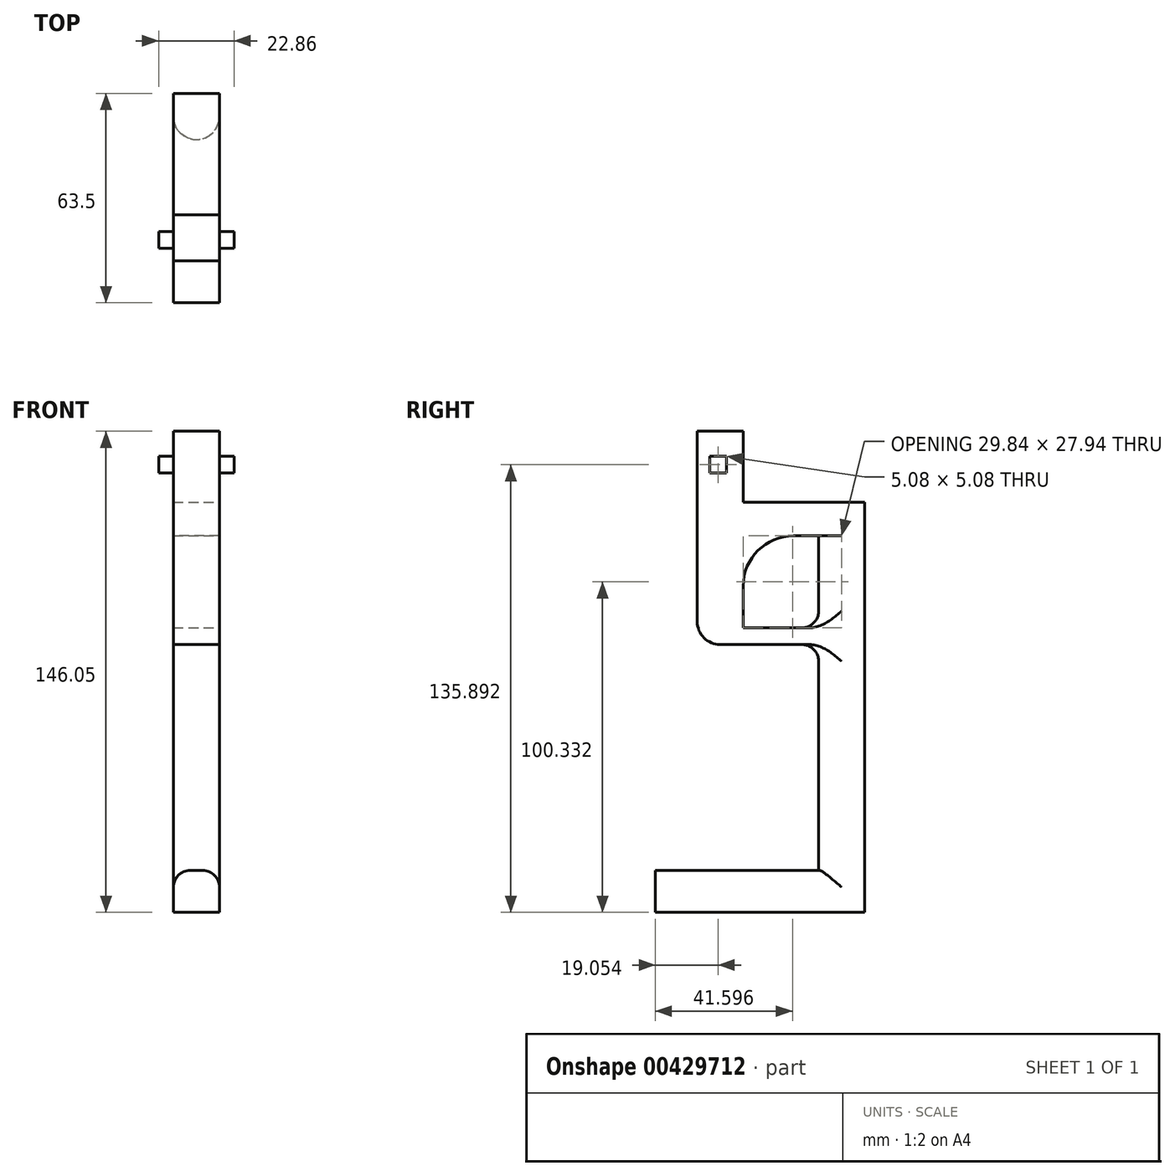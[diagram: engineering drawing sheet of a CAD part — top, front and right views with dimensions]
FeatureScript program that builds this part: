
annotation { "Feature Type Name" : "Feature", "Feature Type Description" : "" }
export const myFeature = defineFeature(function(context is Context, id is Id, definition is map)
    precondition{}
    {
        {
            var Q0;
            Q0=qCreatedBy(makeId("Right.planeOp"),FACE);
            var sketch = newSketch(context, id + "F0", { "sketchPlane" : qUnion([Q0])});
            skLineSegment(sketch, "E0.bottom", {"start": v(-42.7, -17.5) * mm, "end": v(20.8, -17.5) * mm});
            skLineSegment(sketch, "E0.top", {"start": v(-42.7, -30.2) * mm, "end": v(20.8, -30.2) * mm});
            skLineSegment(sketch, "E0.left", {"start": v(-42.7, -17.5) * mm, "end": v(-42.7, -30.2) * mm});
            skLineSegment(sketch, "E0.right", {"start": v(20.8, -17.5) * mm, "end": v(20.8, -30.2) * mm});
            skSolve(sketch);
        }
        {
            var Q0;
            Q0=makeQuery(id+"F0.imprint","IMPRINT",FACE,{"disambiguationData":[TD([[makeQuery(id+"F0.imprint","IMPRINT",EDGE,{"derivedFrom":sQuery(id+"F0.wireOp",EDGE,"E0.bottom")}),-1.0]])]});
            extrude(context, id + "F1", {"entities" : qUnion([Q0]), "endBound" : BoundingType.SYMMETRIC, "depth" : 13.97 * mm});
        }
        {
            var Q0;
            Q0=makeQuery(id+"F1.opExtrude","SWEPT_FACE",FACE,{"disambiguationData":[OSD([sQuery(id+"F0.wireOp",EDGE,"E0.bottom")])]});
            var sketch = newSketch(context, id + "F2", { "sketchPlane" : qUnion([Q0])});
            skCircle(sketch, "E1", {"center": v(0, 13.82) * mm, "radius": 6.99 * mm});
            skSolve(sketch);
        }
        {
            var Q0;
            {var subQ0=sQuery(id+"F2.wireOp",EDGE,"E1");var subQ1=sQuery(id+"F0.wireOp",EDGE,"E0.bottom");var subQ3=makeQuery(id+"F2.imprint","INTERSECT",VERTEX,{"derivedFrom":[makeQuery(id+"F1.opExtrude","CAP_EDGE",EDGE,{"disambiguationData":[OSD([subQ1])],"isStart":false}),subQ0]});Q0=makeQuery(id+"F2.imprint","IMPRINT",FACE,{"disambiguationData":[TD([[makeQuery(id+"F2.imprint","IMPRINT",EDGE,{"disambiguationData":[TD([[subQ3,1.0]])],"derivedFrom":subQ0}),1.0]])]});}
            extrude(context, id + "F3", {"entities" : qUnion([Q0]), "operationType" : NewBodyOperationType.ADD, "depth" : 101.6 * mm});
        }
        {
            var Q0;
            Q0=qCreatedBy(makeId("Right.planeOp"),FACE);
            var sketch = newSketch(context, id + "F4", { "sketchPlane" : qUnion([Q0])});
            skLineSegment(sketch, "E2.bottom", {"start": v(-30, 56.16) * mm, "end": v(20.8, 56.16) * mm});
            skLineSegment(sketch, "E2.top", {"start": v(-30, 51.08) * mm, "end": v(20.8, 51.08) * mm});
            skLineSegment(sketch, "E2.left", {"start": v(-30, 56.16) * mm, "end": v(-30, 51.08) * mm});
            skLineSegment(sketch, "E2.right", {"start": v(20.8, 56.16) * mm, "end": v(20.8, 51.08) * mm});
            skLineSegment(sketch, "E3.bottom", {"start": v(-30, 94.26) * mm, "end": v(20.8, 94.26) * mm});
            skLineSegment(sketch, "E3.top", {"start": v(-30, 84.1) * mm, "end": v(20.8, 84.1) * mm});
            skLineSegment(sketch, "E3.left", {"start": v(-30, 94.26) * mm, "end": v(-30, 84.1) * mm});
            skLineSegment(sketch, "E3.right", {"start": v(20.8, 94.26) * mm, "end": v(20.8, 84.1) * mm});
            skSolve(sketch);
        }
        {
            var Q0;
            Q0=makeQuery(id+"F4.imprint","IMPRINT",FACE,{"disambiguationData":[TD([[makeQuery(id+"F4.imprint","IMPRINT",EDGE,{"derivedFrom":sQuery(id+"F4.wireOp",EDGE,"E2.bottom")}),-1.0]])]});
            var Q1;
            Q1=makeQuery(id+"F4.imprint","IMPRINT",FACE,{"disambiguationData":[TD([[makeQuery(id+"F4.imprint","IMPRINT",EDGE,{"derivedFrom":sQuery(id+"F4.wireOp",EDGE,"E3.bottom")}),-1.0]])]});
            extrude(context, id + "F5", {"entities" : qUnion([Q0, Q1]), "operationType" : NewBodyOperationType.ADD, "endBound" : BoundingType.SYMMETRIC, "depth" : 13.97 * mm});
        }
        {
            var Q0;
            Q0=makeQuery(id+"F5.opExtrude","SWEPT_FACE",FACE,{"disambiguationData":[OSD([sQuery(id+"F4.wireOp",EDGE,"E3.bottom")])]});
            var sketch = newSketch(context, id + "F6", { "sketchPlane" : qUnion([Q0])});
            skLineSegment(sketch, "E4.bottom", {"start": v(6.99, -30) * mm, "end": v(-6.99, -30) * mm});
            skLineSegment(sketch, "E4.top", {"start": v(6.99, -16.03) * mm, "end": v(-6.99, -16.03) * mm});
            skLineSegment(sketch, "E4.left", {"start": v(6.99, -30) * mm, "end": v(6.98, -16.03) * mm});
            skLineSegment(sketch, "E4.right", {"start": v(-6.99, -30) * mm, "end": v(-6.99, -16.03) * mm});
            skSolve(sketch);
        }
        {
            var Q0;
            Q0=makeQuery(id+"F6.imprint","IMPRINT",FACE,{"disambiguationData":[TD([[makeQuery(id+"F6.imprint","IMPRINT",EDGE,{"derivedFrom":sQuery(id+"F6.wireOp",EDGE,"E4.bottom")}),-1.0]])]});
            var Q1;
            {var subQ0=sQuery(id+"F4.wireOp",EDGE,"E2.right");var subQ1=sQuery(id+"F4.wireOp",EDGE,"E2.left");var subQ2=sQuery(id+"F4.wireOp",EDGE,"E2.top");var subQ3=sQuery(id+"F4.wireOp",EDGE,"E2.bottom");var subQ4=makeQuery(id+"F5.opExtrude","SWEPT_FACE",FACE,{"disambiguationData":[OSD([subQ3])]});Q1=makeQuery(id+"F5.boolean.opBoolean","SPLIT",FACE,{"disambiguationData":[TD([makeQuery(id+"F3.opExtrude","SWEPT_FACE",FACE,{"disambiguationData":[OSD([sQuery(id+"F2.wireOp",EDGE,"E1")])]}),subQ4,makeQuery(id+"F5.opExtrude","CAP_FACE",FACE,{"disambiguationData":[OSD([subQ3,subQ2,subQ1,subQ0])],"isStart":true}),makeQuery(id+"F5.opExtrude","CAP_FACE",FACE,{"disambiguationData":[OSD([subQ3,subQ2,subQ1,subQ0])],"isStart":false}),makeQuery(id+"F5.opExtrude","SWEPT_FACE",FACE,{"disambiguationData":[OSD([subQ1])]})])],"derivedFrom":subQ4});}
            extrude(context, id + "F7", {"entities" : qUnion([Q0]), "operationType" : NewBodyOperationType.ADD, "endBound" : BoundingType.UP_TO_SURFACE, "oppositeDirection" : true, "endBoundEntityFace" : qUnion([Q1]), "depth" : 25.4 * mm});
        }
        {
            var Q0;
            Q0=makeQuery(id+"F1.opExtrude","CAP_EDGE",EDGE,{"disambiguationData":[OSD([sQuery(id+"F0.wireOp",EDGE,"E0.right")])],"isStart":false});
            var Q1;
            Q1=makeQuery(id+"F1.opExtrude","CAP_EDGE",EDGE,{"disambiguationData":[OSD([sQuery(id+"F0.wireOp",EDGE,"E0.right")])],"isStart":true});
            var Q2;
            Q2=makeQuery(id+"F5.opExtrude","CAP_EDGE",EDGE,{"disambiguationData":[OSD([sQuery(id+"F4.wireOp",EDGE,"E3.right")])],"isStart":false});
            var Q3;
            Q3=makeQuery(id+"F5.opExtrude","CAP_EDGE",EDGE,{"disambiguationData":[OSD([sQuery(id+"F4.wireOp",EDGE,"E3.right")])],"isStart":true});
            var Q4;
            Q4=makeQuery(id+"F5.opExtrude","CAP_EDGE",EDGE,{"disambiguationData":[OSD([sQuery(id+"F4.wireOp",EDGE,"E2.right")])],"isStart":false});
            var Q5;
            Q5=makeQuery(id+"F5.opExtrude","CAP_EDGE",EDGE,{"disambiguationData":[OSD([sQuery(id+"F4.wireOp",EDGE,"E2.right")])],"isStart":true});
            var Q6;
            Q6=makeQuery(id+"F5.opExtrude","SWEPT_EDGE",EDGE,{"disambiguationData":[OSD([sQuery(id+"F4.wireOp",EDGE,"E2.top"),sQuery(id+"F4.wireOp",EDGE,"E2.left")])]});
            fillet(context, id + "F8", {"entities" : qUnion([Q0, Q1, Q2, Q3, Q4, Q5, Q6]), "radius" : 7 * mm, "tangentPropagation" : true, "allowEdgeOverflow" : false});
        }
        {
            var Q0;
            Q0=makeQuery(id+"F5.boolean.opBoolean","INTERSECT",EDGE,{"disambiguationData":[OD(2.0)],"derivedFrom":[makeQuery(id+"F3.opExtrude","SWEPT_FACE",FACE,{"disambiguationData":[OSD([sQuery(id+"F2.wireOp",EDGE,"E1")])]}),makeQuery(id+"F5.opExtrude","SWEPT_FACE",FACE,{"disambiguationData":[OSD([sQuery(id+"F4.wireOp",EDGE,"E2.bottom")])]})]});
            var Q1;
            {var subQ0=sQuery(id+"F2.wireOp",EDGE,"E1");var subQ1=sQuery(id+"F4.wireOp",EDGE,"E3.right");var subQ2=sQuery(id+"F4.wireOp",EDGE,"E3.left");var subQ3=sQuery(id+"F4.wireOp",EDGE,"E3.top");var subQ4=sQuery(id+"F4.wireOp",EDGE,"E3.bottom");Q1=makeQuery(id+"F5.boolean.opBoolean","SPLIT",EDGE,{"disambiguationData":[TD([makeQuery(id+"F3.opExtrude","SWEPT_FACE",FACE,{"disambiguationData":[OSD([subQ0])]}),makeQuery(id+"F5.opExtrude","CAP_FACE",FACE,{"disambiguationData":[OSD([subQ4,subQ3,subQ2,subQ1])],"isStart":true}),makeQuery(id+"F5.opExtrude","CAP_FACE",FACE,{"disambiguationData":[OSD([subQ4,subQ3,subQ2,subQ1])],"isStart":false}),makeQuery(id+"F5.opExtrude","SWEPT_FACE",FACE,{"disambiguationData":[OSD([subQ3])]})])],"derivedFrom":makeQuery(id+"F3.opExtrude","CAP_EDGE",EDGE,{"disambiguationData":[OSD([subQ0])],"isStart":false})});}
            var Q2;
            Q2=makeQuery(id+"F5.boolean.opBoolean","INTERSECT",EDGE,{"disambiguationData":[OD(2.0)],"derivedFrom":[makeQuery(id+"F3.opExtrude","SWEPT_FACE",FACE,{"disambiguationData":[OSD([sQuery(id+"F2.wireOp",EDGE,"E1")])]}),makeQuery(id+"F5.opExtrude","SWEPT_FACE",FACE,{"disambiguationData":[OSD([sQuery(id+"F4.wireOp",EDGE,"E2.top")])]})]});
            var Q3;
            {var subQ0=sQuery(id+"F0.wireOp",EDGE,"E0.bottom");var subQ1=sQuery(id+"F0.wireOp",EDGE,"E0.left");Q3=makeQuery(id+"F3.boolean.opBoolean","SPLIT",EDGE,{"disambiguationData":[TD([makeQuery(id+"F1.opExtrude","SWEPT_FACE",FACE,{"disambiguationData":[OSD([subQ1])]})])],"derivedFrom":makeQuery(id+"F1.opExtrude","CAP_EDGE",EDGE,{"disambiguationData":[OSD([subQ0])],"isStart":false})});}
            var Q4;
            {var subQ0=sQuery(id+"F0.wireOp",EDGE,"E0.bottom");var subQ1=sQuery(id+"F0.wireOp",EDGE,"E0.left");Q4=makeQuery(id+"F3.boolean.opBoolean","SPLIT",EDGE,{"disambiguationData":[TD([makeQuery(id+"F1.opExtrude","SWEPT_FACE",FACE,{"disambiguationData":[OSD([subQ1])]})])],"derivedFrom":makeQuery(id+"F1.opExtrude","CAP_EDGE",EDGE,{"disambiguationData":[OSD([subQ0])],"isStart":true})});}
            fillet(context, id + "F9", {"entities" : qUnion([Q0, Q1, Q2, Q3, Q4]), "radius" : 5.08 * mm, "tangentPropagation" : true, "allowEdgeOverflow" : false});
        }
        {
            var Q0;
            Q0 = qSketchRegion(id + "F6", true);
            extrude(context, id + "F10", {"entities" : qUnion([Q0]), "operationType" : NewBodyOperationType.ADD, "depth" : 21.59 * mm});
        }
        {
            var Q0;
            Q0=qCreatedBy(makeId("Right.planeOp"),FACE);
            var sketch = newSketch(context, id + "F11", { "sketchPlane" : qUnion([Q0])});
            skLineSegment(sketch, "E5.bottom", {"start": v(-26.19, 108.23) * mm, "end": v(-21.1, 108.23) * mm});
            skLineSegment(sketch, "E5.top", {"start": v(-26.19, 103.15) * mm, "end": v(-21.1, 103.15) * mm});
            skLineSegment(sketch, "E5.left", {"start": v(-26.19, 108.23) * mm, "end": v(-26.19, 103.15) * mm});
            skLineSegment(sketch, "E5.right", {"start": v(-21.1, 108.23) * mm, "end": v(-21.1, 103.15) * mm});
            skSolve(sketch);
        }
        {
            var Q0;
            Q0 = qSketchRegion(id + "F11", true);
            extrude(context, id + "F12", {"entities" : qUnion([Q0]), "operationType" : NewBodyOperationType.ADD, "endBound" : BoundingType.SYMMETRIC, "depth" : 22.86 * mm});
        }
        {
            var Q0;
            Q0=makeQuery(id+"F5.opExtrude","SWEPT_FACE",FACE,{"disambiguationData":[OSD([sQuery(id+"F4.wireOp",EDGE,"E3.bottom")])]});
            var sketch = newSketch(context, id + "F13", { "sketchPlane" : qUnion([Q0])});
            skLineSegment(sketch, "E6.bottom", {"start": v(-6.99, 20.8) * mm, "end": v(6.99, 20.8) * mm});
            skLineSegment(sketch, "E6.top", {"start": v(-6.99, 13.82) * mm, "end": v(6.99, 13.82) * mm});
            skLineSegment(sketch, "E6.left", {"start": v(-6.99, 20.8) * mm, "end": v(-6.99, 13.82) * mm});
            skLineSegment(sketch, "E6.right", {"start": v(6.99, 20.8) * mm, "end": v(6.99, 13.82) * mm});
            skSolve(sketch);
        }
        {
            var Q0;
            Q0 = qSketchRegion(id + "F13", true);
            var Q1;
            Q1=makeQuery(id+"F1.opExtrude","SWEPT_FACE",FACE,{"disambiguationData":[OSD([sQuery(id+"F0.wireOp",EDGE,"E0.top")])]});
            extrude(context, id + "F14", {"entities" : qUnion([Q0]), "operationType" : NewBodyOperationType.ADD, "endBound" : BoundingType.UP_TO_SURFACE, "oppositeDirection" : true, "endBoundEntityFace" : qUnion([Q1]), "depth" : 25.4 * mm});
        }
        {
            var Q0;
            {var subQ0=sQuery(id+"F4.wireOp",EDGE,"E3.top");var subQ1=makeQuery(id+"F5.opExtrude","SWEPT_FACE",FACE,{"disambiguationData":[OSD([subQ0])]});var subQ2=sQuery(id+"F4.wireOp",EDGE,"E3.right");var subQ3=sQuery(id+"F4.wireOp",EDGE,"E3.left");var subQ4=sQuery(id+"F4.wireOp",EDGE,"E3.bottom");Q0=makeQuery(id+"F7.boolean.opBoolean","INTERSECT",EDGE,{"derivedFrom":[makeQuery(id+"F5.boolean.opBoolean","SPLIT",FACE,{"disambiguationData":[TD([makeQuery(id+"F3.opExtrude","SWEPT_FACE",FACE,{"disambiguationData":[OSD([sQuery(id+"F2.wireOp",EDGE,"E1")])]}),makeQuery(id+"F5.opExtrude","CAP_FACE",FACE,{"disambiguationData":[OSD([subQ4,subQ0,subQ3,subQ2])],"isStart":true}),makeQuery(id+"F5.opExtrude","CAP_FACE",FACE,{"disambiguationData":[OSD([subQ4,subQ0,subQ3,subQ2])],"isStart":false}),subQ1,makeQuery(id+"F5.opExtrude","SWEPT_FACE",FACE,{"disambiguationData":[OSD([subQ3])]})])],"derivedFrom":subQ1}),makeQuery(id+"F7.opExtrude","SWEPT_FACE",FACE,{"disambiguationData":[OSD([sQuery(id+"F6.wireOp",EDGE,"E4.top")])]})]});}
            var Q1;
            Q1=makeQuery(id+"F7.opExtrude","CAP_EDGE",EDGE,{"disambiguationData":[OSD([sQuery(id+"F6.wireOp",EDGE,"E4.top")])],"isStart":false});
            fillet(context, id + "F15", {"entities" : qUnion([Q0, Q1]), "radius" : 15.24 * mm, "tangentPropagation" : true, "allowEdgeOverflow" : false});
        }
    });
